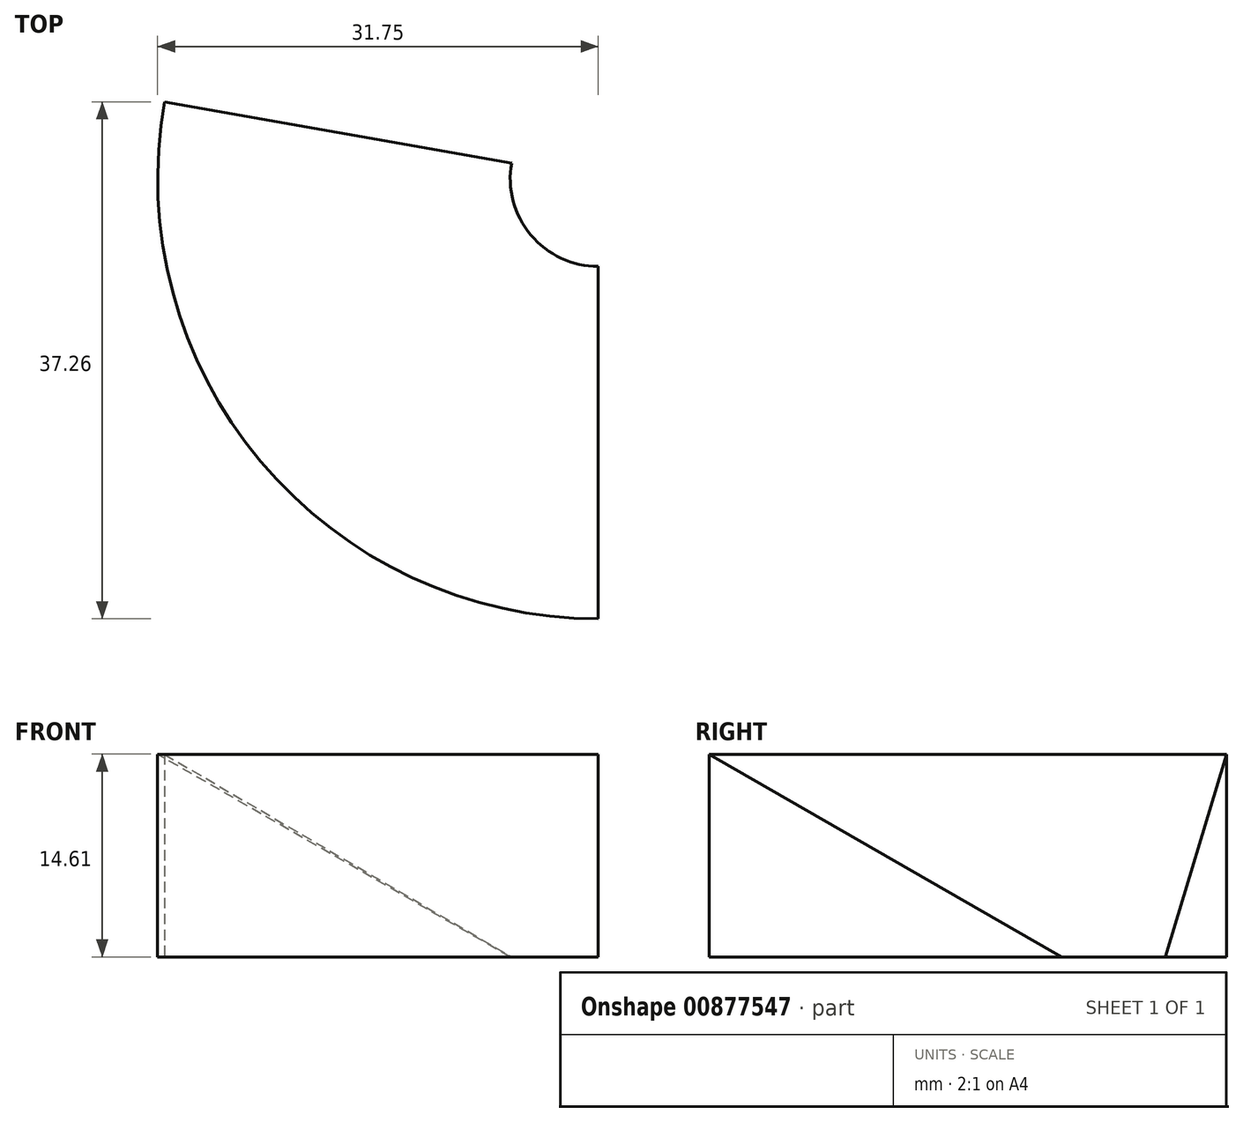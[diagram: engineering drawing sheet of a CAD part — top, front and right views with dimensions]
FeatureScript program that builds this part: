
annotation { "Feature Type Name" : "Feature", "Feature Type Description" : "" }
export const myFeature = defineFeature(function(context is Context, id is Id, definition is map)
    precondition{}
    {
        {
            var Q0;
            Q0=qCreatedBy(makeId("Right.planeOp"),FACE);
            var sketch = newSketch(context, id + "F0", { "sketchPlane" : qUnion([Q0])});
            skLineSegment(sketch, "E0", {"start": v(0, 0) * mm, "end": v(25.4, 0) * mm});
            skLineSegment(sketch, "E1", {"start": v(25.4, 0) * mm, "end": v(25.4, 14.6) * mm});
            skLineSegment(sketch, "E2", {"start": v(25.4, 14.6) * mm, "end": v(0, 0) * mm});
            skLineSegment(sketch, "E3", {"start": v(0, 0) * mm, "end": v(-6.35, 0) * mm, "construction": true});
            skLineSegment(sketch, "E4", {"start": v(-6.35, 0) * mm, "end": v(-6.35, 17.98) * mm, "construction": true});
            skSolve(sketch);
        }
        {
            var Q0;
            Q0=makeQuery(id+"F0.imprint","IMPRINT",FACE,{"disambiguationData":[TD([[makeQuery(id+"F0.imprint","IMPRINT",EDGE,{"derivedFrom":sQuery(id+"F0.wireOp",EDGE,"E0")}),1.0]])]});
            var Q1;
            Q1=sQuery(id+"F0.wireOp",EDGE,"E2");
            var Q2;
            Q2=sQuery(id+"F0.wireOp",EDGE,"E1");
            var Q3;
            Q3=sQuery(id+"F0.wireOp",EDGE,"E0");
            var Q4;
            Q4=sQuery(id+"F0.wireOp",EDGE,"E4");
            revolve(context, id + "F1", {"surfaceOperationType" : NewSurfaceOperationType.NEW, "entities" : qUnion([Q0]), "surfaceEntities" : qUnion([Q1, Q2, Q3]), "axis" : qUnion([Q4]), "revolveType" : RevolveType.FULL});
        }
        {
            var Q0;
            Q0=qCreatedBy(makeId("Top.planeOp"),FACE);
            var sketch = newSketch(context, id + "F2", { "sketchPlane" : qUnion([Q0])});
            skLineSegment(sketch, "E5", {"start": v(0, 0) * mm, "end": v(0, -6.35) * mm, "construction": true});
            skLineSegment(sketch, "E6", {"start": v(0, -6.35) * mm, "end": v(0, -41.74) * mm});
            skLineSegment(sketch, "E7", {"start": v(38.1, -6.35) * mm, "end": v(38.1, -41.74) * mm});
            skLineSegment(sketch, "E8", {"start": v(38.1, -41.74) * mm, "end": v(0, -41.74) * mm});
            skLineSegment(sketch, "E9.top", {"start": v(38.1, 31.75) * mm, "end": v(0, 31.75) * mm});
            skLineSegment(sketch, "E9.left", {"start": v(38.1, -6.35) * mm, "end": v(38.1, 31.75) * mm});
            skLineSegment(sketch, "E9.right", {"start": v(0, -6.35) * mm, "end": v(0, 31.75) * mm});
            skLineSegment(sketch, "E10.bottom", {"start": v(0, -6.35) * mm, "end": v(-6.72, -6.35) * mm, "construction": true});
            skLineSegment(sketch, "E10.top", {"start": v(0, 31.75) * mm, "end": v(-6.72, 31.75) * mm, "construction": true});
            skLineSegment(sketch, "E10.left", {"start": v(0, -6.35) * mm, "end": v(0, 31.75) * mm, "construction": true});
            skLineSegment(sketch, "E10.right", {"start": v(-6.72, -6.35) * mm, "end": v(-6.72, 31.75) * mm, "construction": true});
            skLineSegment(sketch, "E11", {"start": v(0, -6.35) * mm, "end": v(-6.72, 31.75) * mm});
            skLineSegment(sketch, "E12", {"start": v(-6.72, 31.75) * mm, "end": v(0, 31.75) * mm});
            skSolve(sketch);
        }
        {
            var Q0;
            Q0 = qSketchRegion(id + "F2", true);
            extrude(context, id + "F3", {"entities" : qUnion([Q0]), "operationType" : NewBodyOperationType.REMOVE, "endBound" : BoundingType.THROUGH_ALL, "depth" : 25.4 * mm, "offsetDistance" : 25.4 * mm});
        }
        {
            var Q0;
            Q0=qCreatedBy(makeId("Top.planeOp"),FACE);
            var sketch = newSketch(context, id + "F4", { "sketchPlane" : qUnion([Q0])});
            skLineSegment(sketch, "E13", {"start": v(0, 0) * mm, "end": v(0, -6.35) * mm, "construction": true});
            skLineSegment(sketch, "E14.top", {"start": v(0, 27.07) * mm, "end": v(-38.1, 27.07) * mm});
            skLineSegment(sketch, "E14.left", {"start": v(0, -6.35) * mm, "end": v(0, 27.07) * mm});
            skLineSegment(sketch, "E14.right", {"start": v(-38.1, 0.37) * mm, "end": v(-38.1, 27.07) * mm});
            skLineSegment(sketch, "E15", {"start": v(0, -6.35) * mm, "end": v(-38.1, 0.37) * mm});
            skSolve(sketch);
        }
        {
            var Q0;
            Q0 = qSketchRegion(id + "F4", true);
            extrude(context, id + "F5", {"entities" : qUnion([Q0]), "operationType" : NewBodyOperationType.REMOVE, "endBound" : BoundingType.THROUGH_ALL, "depth" : 25.4 * mm, "offsetDistance" : 25.4 * mm});
        }
    });
